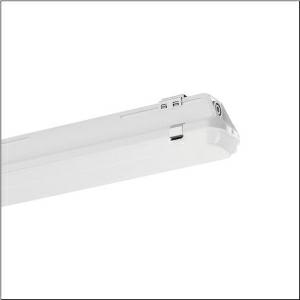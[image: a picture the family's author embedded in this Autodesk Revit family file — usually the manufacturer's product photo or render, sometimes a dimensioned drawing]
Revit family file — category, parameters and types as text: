
# Revit family: monsun_r__11_51fp108p430h_5d5d
name_source: partatom
category: Lighting Fixtures
units: mm (PartAtom-declared; Revit-internal decimal feet)

## family parameters
Cut with Voids When Loaded = No
Host = Face
Light Source = No
Part Type = Normal
Room Calculation Point = No
Round Connector Dimension = Use Diameter
Shared = No

## types (1)
- Monsun® 11 (1 x LED, 3970 lm, 22.2 W, 4000K)
    Apparent Load = 22 VA
    CIE Flux Codes = 47 77 93 94 100
    Color Rendering = 80
    Color Temperature = 4000K
    Default Elevation = 1800 mm
    Description = Monsun® 11, damp-proof luminaire, chain hanger, primary optical cover: enclosure, of PMMA, light emission: direct distribution, primary light characteristic: symmetric, installation type: suspended mounting, surface-mounted, horizontal mounting, vertical mounting, LED, rated luminous flux: 3.970lm, luminous efficacy: 179lm/W, light colour: 840, colour temperature: 4000K, control gear: ON/OFF, with terminal, 3-pole, max. 2.5mm², mains connection: 220..240V, AC, 50/60Hz, rated input power: 22W, luminaire housing, of glass-fibre reinforced polyester, uncoated, bright grey, incl. chain hanger, length: 1.590mm, width: 90mm, height: 88mm, clip for enclosure, of stainless steel (V2A), ceiling mounting element, of stainless steel (V2A), chain hanger, of stainless steel (V2A), protection rating (complete): IP66, insulation class (complete): insulation class I (protective earthing), certification: CE, ENEC, VDE, UKCA, protection symbol: D, impact resistance: IK04, permissible operating ambient temperature: -35..+40°C, standard: EN 50419, EN 60598-2-1, no direct snow, no direct sun, no direct rain, for indoor or canopied outdoor use, corresponds to IFS (International Featured Standards) requirements for safety and quality in the food industry, contact your sales advisor before using the luminaires in applications with unclear chemical exposure, large temperature fluctuations or condensation-forming humidity, LABS conformity tested according to VDMA 24364:2018-05, packaging unit: 1 piece
    Height = 89 mm
    Lamp = 1 x LED
    Lamp Light Flux = 3970 lm
    Lamp Power = 22.2 W
    Lamp count = 1
    Length = 1590 mm
    Luminous efficacy = 179 lm/W
    Manufacturer = Siteco
    ModVariant = No
    Model = 51FP108P430H
    Mounting Place = Ceiling
    Mounting Type = Surface mounted
    Number of Poles = 1
    OnlyDefault = Yes
    Power Factor = 1
    Product Name = Monsun® 11
    Product group = damp-proof luminaire
    ProductGroupID = 301
    Protection Class = Protection class I
    Protection Degree = IP 66
    RLX_Detail_Level = 1
    RLX_Emergency_Light_Flux = 0 lm
    RLX_Emergency_Type = 0
    RLX_Emergency_Type_DB = No
    RlxData = <blob elided: 88497 chars, md5=8f69e559>
    Socket = socket
    Standby Power = 0 W
    System Light Flux = 3970 lm
    System Power = 22 W
    Type Comments = Product without accessories
    Type Image = l_1349237.jpg
    URL = http://relux.com
    VarID = ---
    Voltage = 0 V
    Weight = 0.00 kg
    Width = 90 mm

## geometry (parser evidence)
native form markers: Blend x4, Sweep x15
no freeform markers — native parametric forms only
